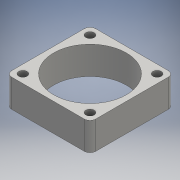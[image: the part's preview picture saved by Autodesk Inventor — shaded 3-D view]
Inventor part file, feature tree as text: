
AUTODESK INVENTOR PART (.ipt)
format: ipt  version: 2016 SP1 (Build 200210100, 210)  size: 120,832 bytes
history: native  units: mm
features: extrude x1, fillet x1, sketch x1
ambient origin geometry x8: Origin, YZ Plane, XZ Plane, XY Plane, X Axis, Y Axis, Z Axis, Center Point
bodies: Solid1 (feature_tree)
feature tree (3):
  extrude  "Extrusion1"  Depth=30.0mm
  fillet  "Fillet1"  Radius=15.0mm
  sketch  "Sketch1"  dims[d0=30.0mm d1=30.0mm d2=15.0mm d3=15.0mm d4=26.0mm d5=3.0mm d6=3.0mm d7=3.0mm d8=40.0mm d10=360.0deg d12=10.0mm d13=0.0mm d14=2.0mm]
